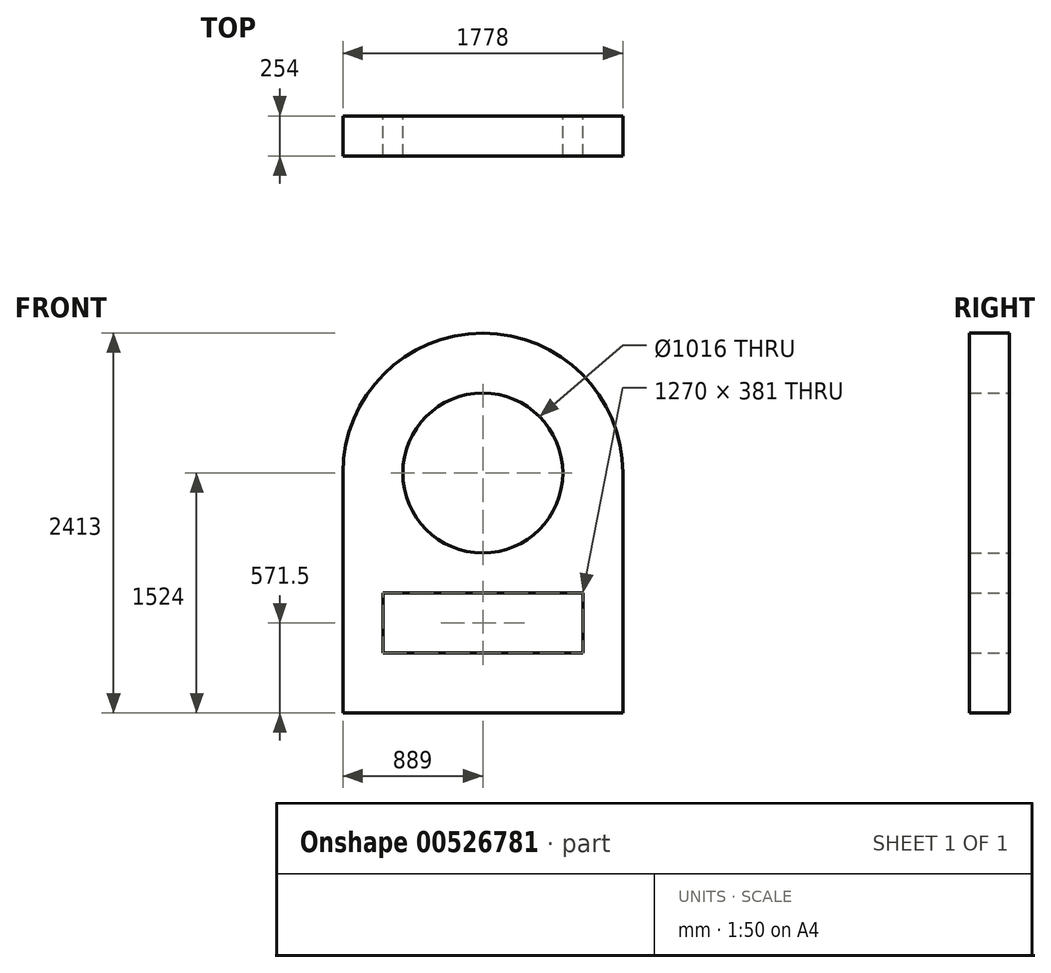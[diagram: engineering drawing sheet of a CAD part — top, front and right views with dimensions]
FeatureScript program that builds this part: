
annotation { "Feature Type Name" : "Feature", "Feature Type Description" : "" }
export const myFeature = defineFeature(function(context is Context, id is Id, definition is map)
    precondition{}
    {
        {
            var Q0;
            Q0=qCreatedBy(makeId("Front.planeOp"),FACE);
            var sketch = newSketch(context, id + "F0", { "sketchPlane" : qUnion([Q0])});
            skLineSegment(sketch, "E0", {"start": v(0, 0) * mm, "end": v(1778, 0) * mm});
            skLineSegment(sketch, "E1", {"start": v(1778, 0) * mm, "end": v(1778, 1524) * mm});
            skLineSegment(sketch, "E2", {"start": v(0, 0) * mm, "end": v(0, 1524) * mm});
            skArc(sketch, "E3", {"start": v(1778, 1524) * mm, "mid": v(889, 2413) * mm, "end": v(0, 1524) * mm});
            skCircle(sketch, "E4", {"center": v(889, 1524) * mm, "radius": 508 * mm});
            skLineSegment(sketch, "E5", {"start": v(254, 381) * mm, "end": v(254, 762) * mm});
            skLineSegment(sketch, "E6", {"start": v(254, 762) * mm, "end": v(1524, 762) * mm});
            skLineSegment(sketch, "E7", {"start": v(1524, 762) * mm, "end": v(1524, 381) * mm});
            skLineSegment(sketch, "E8", {"start": v(1524, 381) * mm, "end": v(254, 381) * mm});
            skSolve(sketch);
        }
        {
            var Q0;
            Q0 = qSketchRegion(id + "F0", true);
            extrude(context, id + "F1", {"entities" : qUnion([Q0]), "depth" : 254 * mm, "offsetDistance" : 25.4 * mm});
        }
    });
